# Revit family: VF3_DN125-DN150_AMV(E) 85(86)_RFA_1
name_source: partatom
category: Pipe Accessories
units: mm (PartAtom-declared; Revit-internal decimal feet)

## family parameters
Always vertical = Yes
Cut with Voids When Loaded = No
OmniClass Number = 23.65.55.14.17
OmniClass Title = Adjusting/Controlling Valves for Liquid Services
Part Type = Valve - Breaks Into
Round Connector Dimension = Use Diameter
Shared = No
Work Plane-Based = No

## types (2) — shared parameters
082G1450 = AMV(E) 85(86)_RFA : AMV 85_24V_082G1450
082G1451 = AMV(E) 85(86)_RFA : AMV 85_230V_082G1451
082G1460 = AMV(E) 85(86)_RFA : AMV 86_24V_082G1460
082G1461 = AMV(E) 85(86)_RFA : AMV 86_230V_082G1461
082G1462 = AMV(E) 85(86)_RFA : AME 86_24V_082G1462
Actuator Type = AMV(E) 85(86)_RFA : AMV 85_24V_082G1450
Connection = Flange
Description = Motorized Control Valve
Flange Depth = 26 mm
H1_2 = 185 mm
IfcExportAs = IfcValveType
IfcExportType = VF3
LOD 200 = No
LOD 350 = Yes
Loss Method = Not Defined
Manufacturer = Danfoss
Max Medium Temperature = 200°C
Min Medium Temperature = -10°C
Power = 11 VA
Pressure Stage = PN 16
R1 = 40 mm  [stored 0.131234 ft]
R1_1 = 32 mm  [stored 0.104987 ft]
R_Top 2 = 25 mm  [stored 0.082021 ft]
Stroke = 40 mm
TC = 10 mm  [stored 0.0328084 ft]
URL = https://store.danfoss.com
Valve Body Material = Danfoss Ductile Iron
Voltage = 24 V
zero-valued in all types: K Coefficient

## per-type parameters (varying)
- VF3_DN150_Kv320_065B3150: A1_Flow Pipe Path=161.50°; A2_Flow Pipe Path=156.00°; Arc_Top Offset=145 mm; Body Bottom Offset=200 mm; Body Top Offset=150 mm; D=150 mm; DN=150; Ext2_Depth=12 mm  [stored 0.0393701 ft]; Ext_Depth=-100 mm  [stored -0.328084 ft]; H1=281.5 mm; H1_1=112 mm  [stored 0.367454 ft]; H2=300 mm; H2_1=30 mm  [stored 0.0984252 ft]; H2_1_ve=-30 mm  [stored -0.0984252 ft]; H2_2=30 mm  [stored 0.0984252 ft]; H2_3=150 mm; H_1=25 mm  [stored 0.082021 ft]; H_Blend=31 mm  [stored 0.101706 ft]; H_Flow pipe1=65 mm  [stored 0.213255 ft]; Kvs=320.00 m³/h; L=480 mm; L_B=61.35 mm; Model=065B3150; Model Type=VF3_DN150_Kv320; R1_Bottom2=95 mm  [stored 0.31168 ft]; R1_Bottom3=100 mm  [stored 0.328084 ft]; R1_Flow Pipe1=60 mm  [stored 0.19685 ft]; R2_Bottom2=85 mm  [stored 0.278871 ft]; R2_Bottom3=110 mm  [stored 0.360892 ft]; R2_Flow Pipe1=85 mm  [stored 0.278871 ft]; R3_Flow Pipe1=95 mm  [stored 0.31168 ft]; R_Body=130 mm; R_Body Bottom=116 mm  [stored 0.380577 ft]; R_Body Top=97 mm  [stored 0.318241 ft]; R_Bottom=132 mm; R_Bottom1=97 mm  [stored 0.318241 ft]; R_Connection=108  [stored 0.354331 ft]; R_Flange=142; R_Flow Pipe1=62 mm  [stored 0.203412 ft]; R_Flow Pipe2=85  [stored 0.278871 ft]; R_Top=10 mm  [stored 0.0328084 ft]; TH2=228 mm; W=284 mm; Weight=92.00 kg
- VF3_DN125_Kv220_065B3125: A1_Flow Pipe Path=159.00°; A2_Flow Pipe Path=159.00°; Arc_Top Offset=140 mm; Body Bottom Offset=170 mm; Body Top Offset=145 mm; D=125 mm  [stored 0.410105 ft]; DN=125  [stored 0.410105 ft]; Ext2_Depth=18 mm  [stored 0.0590551 ft]; Ext_Depth=-50 mm  [stored -0.164042 ft]; H1=305 mm; H1_1=100 mm  [stored 0.328084 ft]; H2=250 mm; H2_1=29 mm  [stored 0.0951444 ft]; H2_1_ve=-25 mm  [stored -0.082021 ft]; H2_2=25 mm  [stored 0.082021 ft]; H2_3=105 mm  [stored 0.344488 ft]; H_1=30 mm  [stored 0.0984252 ft]; H_Blend=29 mm  [stored 0.0951444 ft]; H_Flow pipe1=59 mm; Kvs=220.00 m³/h; L=400 mm; L_B=35 mm  [stored 0.114829 ft]; Model=065B3125; Model Type=VF3_DN125_Kv220; R1_Bottom2=80 mm  [stored 0.262467 ft]; R1_Bottom3=88 mm  [stored 0.288714 ft]; R1_Flow Pipe1=53 mm  [stored 0.173885 ft]; R2_Bottom2=72 mm  [stored 0.23622 ft]; R2_Bottom3=95 mm  [stored 0.31168 ft]; R2_Flow Pipe1=70 mm  [stored 0.229659 ft]; R3_Flow Pipe1=82 mm  [stored 0.269029 ft]; R_Body=110 mm  [stored 0.360892 ft]; R_Body Bottom=95 mm  [stored 0.31168 ft]; R_Body Top=80 mm  [stored 0.262467 ft]; R_Bottom=117 mm  [stored 0.383858 ft]; R_Bottom1=85 mm  [stored 0.278871 ft]; R_Connection=93  [stored 0.305118 ft]; R_Flange=125  [stored 0.410105 ft]; R_Flow Pipe1=50 mm  [stored 0.164042 ft]; R_Flow Pipe2=72  [stored 0.23622 ft]; R_Top=7 mm  [stored 0.0229659 ft]; TH2=178 mm; W=250 mm; Weight=65.30 kg

note: [stored X ft] marks values corroborated as IEEE doubles in the binary element streams (Revit-internal decimal feet)

## geometry (parser evidence)
native form markers: Blend x1, Sweep x5
no freeform markers — native parametric forms only
